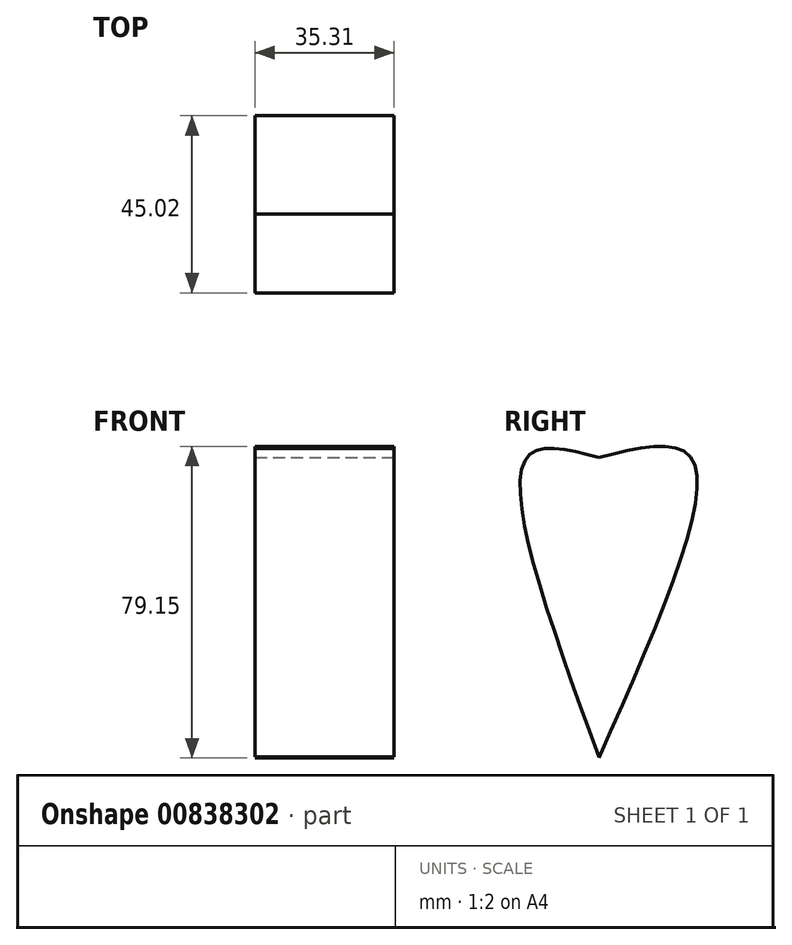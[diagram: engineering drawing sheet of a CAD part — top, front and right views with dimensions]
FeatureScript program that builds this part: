
annotation { "Feature Type Name" : "Feature", "Feature Type Description" : "" }
export const myFeature = defineFeature(function(context is Context, id is Id, definition is map)
    precondition{}
    {
        {
            var Q0;
            Q0=qCreatedBy(makeId("Right.planeOp"),FACE);
            var sketch = newSketch(context, id + "F0", { "sketchPlane" : qUnion([Q0])});
            skFitSpline(sketch, "E0", {"points": [v(0, 0) * mm, v(-18.24, 0) * mm, v(0, -76.12) * mm], "startDerivative": vector(-69.55, 18.37) * mm, "endDerivative": vector(55.06, -150.93) * mm});
            skSolve(sketch);
        }
        {
            var Q0;
            Q0=qCreatedBy(makeId("Right.planeOp"),FACE);
            var sketch = newSketch(context, id + "F1", { "sketchPlane" : qUnion([Q0])});
            skFitSpline(sketch, "E1", {"points": [v(0, 0) * mm, v(23.37, 0) * mm, v(0, -76.36) * mm], "startDerivative": vector(84.58, 20.66) * mm, "endDerivative": vector(-69.3, -155.85) * mm});
            skSolve(sketch);
        }
        {
            var Q0;
            Q0=sQuery(id+"F1.wireOp",EDGE,"E1");
            var Q1;
            Q1=sQuery(id+"F0.wireOp",EDGE,"E0");
            extrude(context, id + "F2", {"bodyType" : ToolBodyType.SURFACE, "surfaceEntities" : qUnion([Q0, Q1]), "depth" : 35.3 * mm, "offsetDistance" : 25.4 * mm});
        }
    });
